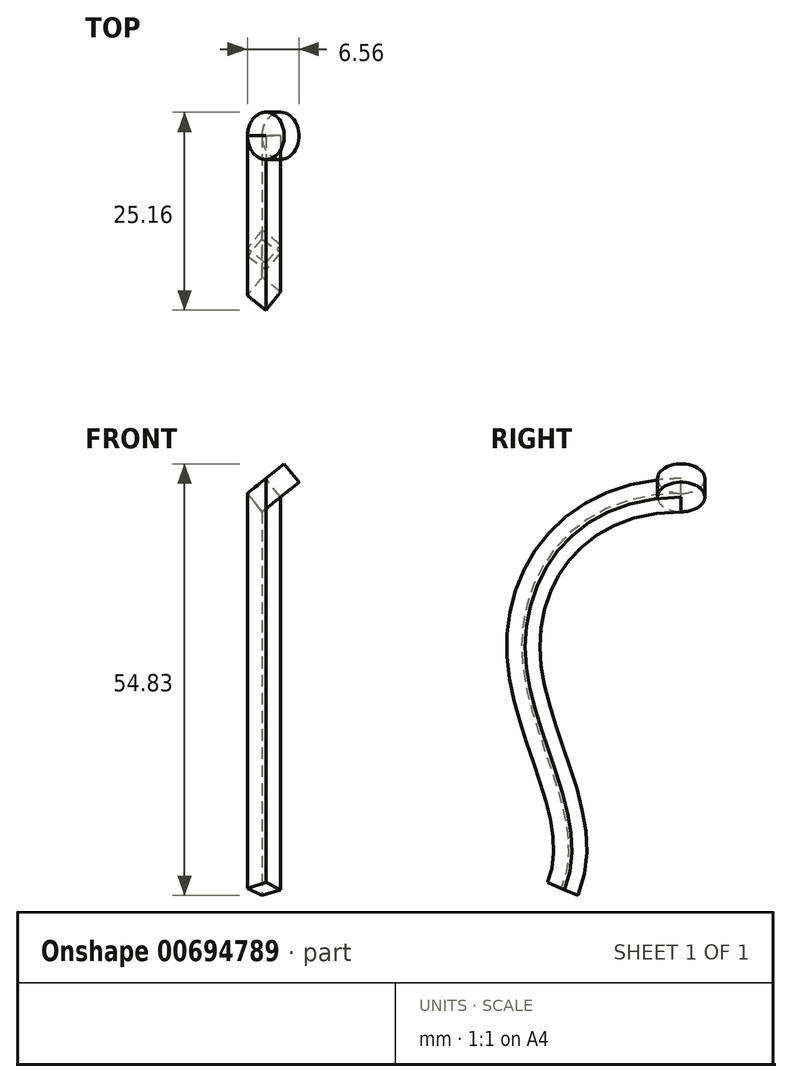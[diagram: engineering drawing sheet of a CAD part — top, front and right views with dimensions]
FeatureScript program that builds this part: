
annotation { "Feature Type Name" : "Feature", "Feature Type Description" : "" }
export const myFeature = defineFeature(function(context is Context, id is Id, definition is map)
    precondition{}
    {
        {
            var Q0;
            Q0=qCreatedBy(makeId("Right.planeOp"),FACE);
            var sketch = newSketch(context, id + "F0", { "sketchPlane" : qUnion([Q0])});
            skLineSegment(sketch, "E0", {"start": v(0, 0) * mm, "end": v(0, -50) * mm});
            skLineSegment(sketch, "E1", {"start": v(0, -50) * mm, "end": v(-15, -50) * mm});
            skFitSpline(sketch, "E2", {"points": [v(-15, -50) * mm, v(-20, -20) * mm, v(0, 0) * mm], "startDerivative": vector(21.86, 52.17) * mm, "endDerivative": vector(82.68, 0) * mm});
            skSolve(sketch);
        }
        {
            var Q0;
            Q0=qCreatedBy(makeId("Front.planeOp"),FACE);
            var sketch = newSketch(context, id + "F1", { "sketchPlane" : qUnion([Q0])});
            skLineSegment(sketch, "E3.bottom", {"start": v(-0.46, -2.07) * mm, "end": v(-2.34, 0.26) * mm});
            skLineSegment(sketch, "E3.top", {"start": v(1.88, -0.2) * mm, "end": v(0, 2.15) * mm});
            skLineSegment(sketch, "E3.left", {"start": v(-0.46, -2.07) * mm, "end": v(1.88, -0.2) * mm});
            skLineSegment(sketch, "E3.right", {"start": v(-2.34, 0.26) * mm, "end": v(0, 2.15) * mm});
            skPoint(sketch, "E3.middle", {"position": v(-0.23, 0.04) * mm});
            skSolve(sketch);
        }
        {
            var Q0;
            Q0=makeQuery(id+"F1.imprint","IMPRINT",FACE,{"disambiguationData":[TD([[makeQuery(id+"F1.imprint","IMPRINT",EDGE,{"derivedFrom":sQuery(id+"F1.wireOp",EDGE,"E3.bottom")}),-1.0]])]});
            var Q1;
            Q1=sQuery(id+"F0.wireOp",EDGE,"E2");
            sweep(context, id + "F2", {"profiles" : qUnion([Q0]), "path" : qUnion([Q1])});
        }
        {
            var Q0;
            Q0=makeQuery(id+"F1.imprint","IMPRINT",FACE,{"disambiguationData":[TD([[makeQuery(id+"F1.imprint","IMPRINT",EDGE,{"derivedFrom":sQuery(id+"F1.wireOp",EDGE,"E3.bottom")}),-1.0]])]});
            var Q1;
            Q1=sQuery(id+"F1.wireOp",EDGE,"E3.top");
            revolve(context, id + "F3", {"entities" : qUnion([Q0]), "axis" : qUnion([Q1]), "revolveType" : RevolveType.FULL});
        }
    });
